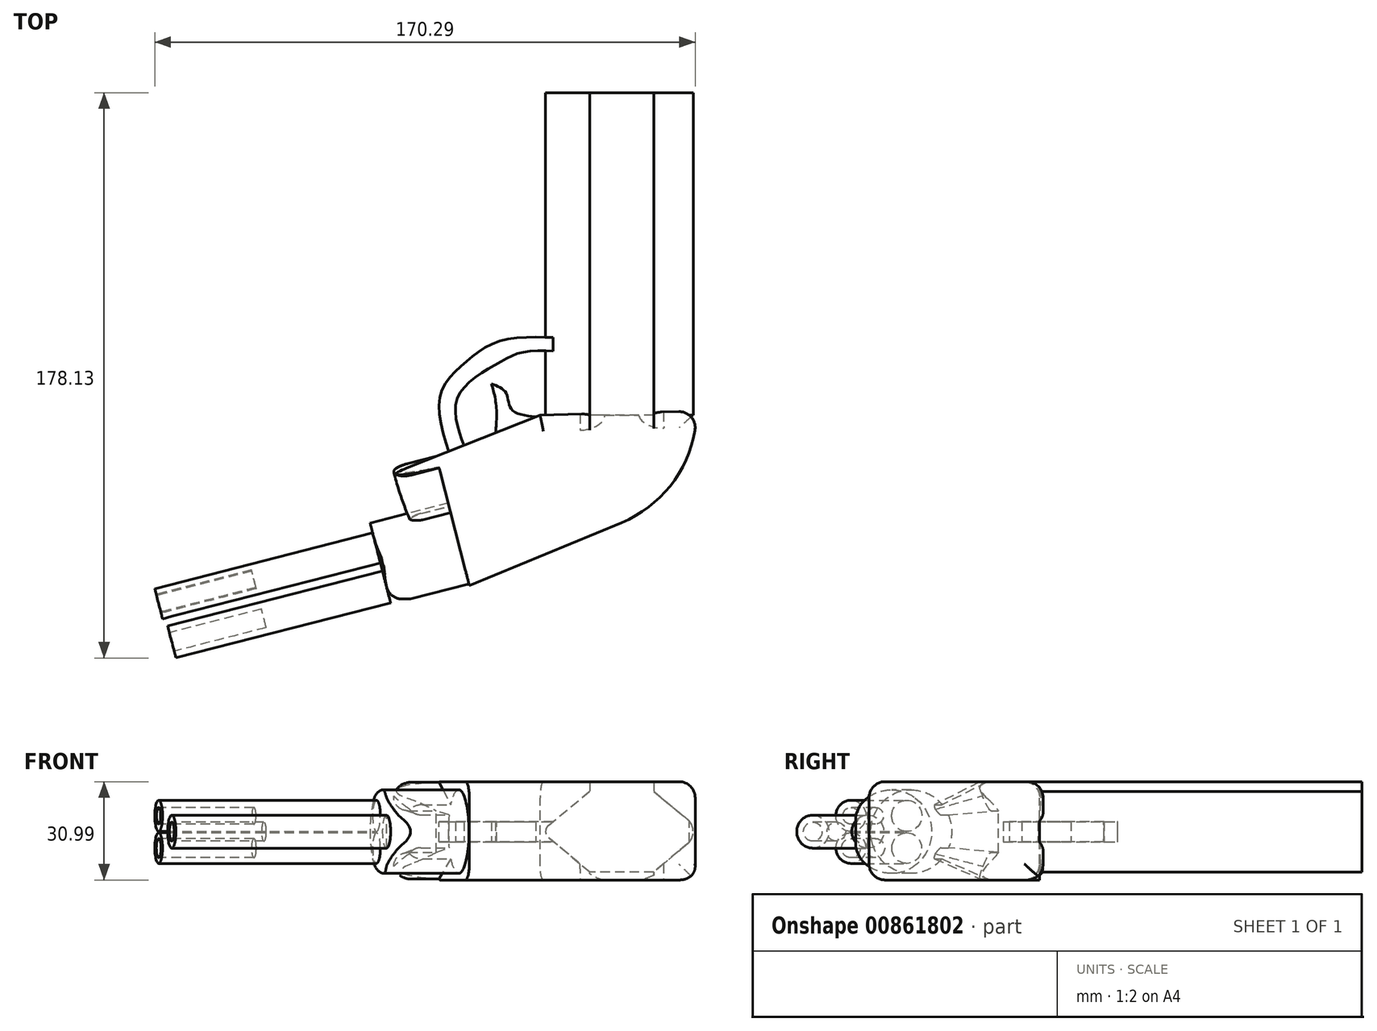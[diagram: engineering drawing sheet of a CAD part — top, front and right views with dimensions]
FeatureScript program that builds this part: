
annotation { "Feature Type Name" : "Feature", "Feature Type Description" : "" }
export const myFeature = defineFeature(function(context is Context, id is Id, definition is map)
    precondition{}
    {
        {
            var Q0;
            Q0=qCreatedBy(makeId("Front.planeOp"),FACE);
            var sketch = newSketch(context, id + "F0", { "sketchPlane" : qUnion([Q0])});
            skLineSegment(sketch, "E0", {"start": v(-10.1, 12.7) * mm, "end": v(10.1, 12.7) * mm});
            skLineSegment(sketch, "E1", {"start": v(10.1, 12.7) * mm, "end": v(25.4, 0) * mm});
            skLineSegment(sketch, "E2", {"start": v(25.4, 0) * mm, "end": v(10.1, -12.7) * mm});
            skLineSegment(sketch, "E3", {"start": v(10.1, -12.7) * mm, "end": v(-10.1, -12.7) * mm});
            skLineSegment(sketch, "E4", {"start": v(-10.1, -12.7) * mm, "end": v(-25.4, 0) * mm});
            skLineSegment(sketch, "E5", {"start": v(-25.4, 0) * mm, "end": v(-10.1, 12.7) * mm});
            skLineSegment(sketch, "E6", {"start": v(0, 12.7) * mm, "end": v(0, -12.7) * mm, "construction": true});
            skLineSegment(sketch, "E7", {"start": v(-25.4, 0) * mm, "end": v(25.4, 0) * mm, "construction": true});
            skSolve(sketch);
        }
        {
            var Q0;
            Q0=makeQuery(id+"F0.imprint","IMPRINT",FACE,{"disambiguationData":[TD([[makeQuery(id+"F0.imprint","IMPRINT",EDGE,{"derivedFrom":sQuery(id+"F0.wireOp",EDGE,"E0")}),-1.0]])]});
            extrude(context, id + "F1", {"entities" : qUnion([Q0]), "depth" : 101.6 * mm, "offsetDistance" : 25.4 * mm});
        }
        {
            var Q0;
            Q0=makeQuery(id+"F1.opExtrude","SWEPT_FACE",FACE,{"disambiguationData":[OSD([sQuery(id+"F0.wireOp",EDGE,"E0")])]});
            var sketch = newSketch(context, id + "F2", { "sketchPlane" : qUnion([Q0])});
            skLineSegment(sketch, "E8", {"start": v(-25.7, -101.58) * mm, "end": v(-77.82, -122.29) * mm});
            skLineSegment(sketch, "E9", {"start": v(-77.82, -122.29) * mm, "end": v(-81.03, -128.71) * mm});
            skLineSegment(sketch, "E10", {"start": v(-81.03, -128.71) * mm, "end": v(-73.12, -159.56) * mm});
            skLineSegment(sketch, "E11", {"start": v(-73.12, -159.56) * mm, "end": v(-58.16, -159.56) * mm});
            skLineSegment(sketch, "E12", {"start": v(-58.16, -159.56) * mm, "end": v(0, -135.46) * mm});
            skArc(sketch, "E13", {"start": v(0, -135.46) * mm, "mid": v(17.1, -121.47) * mm, "end": v(23.63, -100.35) * mm});
            skLineSegment(sketch, "E14", {"start": v(-25.7, -101.58) * mm, "end": v(23.63, -100.35) * mm});
            skSolve(sketch);
        }
        {
            var Q0;
            Q0=makeQuery(id+"F2.imprint","IMPRINT",FACE,{"disambiguationData":[TD([[makeQuery(id+"F2.imprint","IMPRINT",EDGE,{"derivedFrom":sQuery(id+"F2.wireOp",EDGE,"E8")}),1.0]])]});
            extrude(context, id + "F3", {"entities" : qUnion([Q0]), "operationType" : NewBodyOperationType.ADD, "oppositeDirection" : true, "depth" : 27.94 * mm, "offsetDistance" : 25.4 * mm});
        }
        {
            var Q0;
            Q0=makeQuery(id+"F3.opExtrude","CAP_FACE",FACE,{"disambiguationData":[OSD([sQuery(id+"F2.wireOp",EDGE,"E8"),sQuery(id+"F2.wireOp",EDGE,"E9"),sQuery(id+"F2.wireOp",EDGE,"E10"),sQuery(id+"F2.wireOp",EDGE,"E11"),sQuery(id+"F2.wireOp",EDGE,"E12"),sQuery(id+"F2.wireOp",EDGE,"E13"),sQuery(id+"F2.wireOp",EDGE,"E14")])],"isStart":true});
            extrude(context, id + "F4", {"entities" : qUnion([Q0]), "operationType" : NewBodyOperationType.ADD, "depth" : 3.05 * mm, "offsetDistance" : 25.4 * mm});
        }
        {
            var Q0;
            Q0=makeQuery(id+"F4.opExtrude","CAP_EDGE",EDGE,{"disambiguationData":[OSD([sQuery(id+"F2.wireOp",EDGE,"E14")])],"isStart":false});
            var Q1;
            Q1=makeQuery(id+"F4.opExtrude","CAP_EDGE",EDGE,{"disambiguationData":[OSD([sQuery(id+"F2.wireOp",EDGE,"E13")])],"isStart":false});
            var Q2;
            Q2=makeQuery(id+"F4.opExtrude","CAP_EDGE",EDGE,{"disambiguationData":[OSD([sQuery(id+"F2.wireOp",EDGE,"E8")])],"isStart":false});
            var Q3;
            Q3=makeQuery(id+"F4.opExtrude","CAP_EDGE",EDGE,{"disambiguationData":[OSD([sQuery(id+"F2.wireOp",EDGE,"E10")])],"isStart":false});
            var Q4;
            {var subQ0=sQuery(id+"F2.wireOp",EDGE,"E14");var subQ1=sQuery(id+"F2.wireOp",EDGE,"E13");Q4=makeQuery(id+"F4.boolean.opBoolean","MERGE",EDGE,{"derivedFrom":[makeQuery(id+"F3.opExtrude","SWEPT_EDGE",EDGE,{"disambiguationData":[OSD([subQ1,subQ0])]}),makeQuery(id+"F4.opExtrude","SWEPT_EDGE",EDGE,{"disambiguationData":[OSD([subQ1,subQ0])]})]});}
            var Q5;
            Q5=makeQuery(id+"F3.opExtrude","CAP_EDGE",EDGE,{"disambiguationData":[OSD([sQuery(id+"F2.wireOp",EDGE,"E14")])],"isStart":false});
            var Q6;
            Q6=makeQuery(id+"F3.opExtrude","CAP_EDGE",EDGE,{"disambiguationData":[OSD([sQuery(id+"F2.wireOp",EDGE,"E13")])],"isStart":false});
            var Q7;
            Q7=makeQuery(id+"F3.opExtrude","CAP_EDGE",EDGE,{"disambiguationData":[OSD([sQuery(id+"F2.wireOp",EDGE,"E10")])],"isStart":false});
            var Q8;
            Q8=makeQuery(id+"F3.opExtrude","CAP_EDGE",EDGE,{"disambiguationData":[OSD([sQuery(id+"F2.wireOp",EDGE,"E8")])],"isStart":false});
            var Q9;
            {var subQ0=sQuery(id+"F2.wireOp",EDGE,"E11");Q9=makeQuery(id+"F4.boolean.opBoolean","MERGE",FACE,{"derivedFrom":[makeQuery(id+"F3.opExtrude","SWEPT_FACE",FACE,{"disambiguationData":[OSD([subQ0])]}),makeQuery(id+"F4.opExtrude","SWEPT_FACE",FACE,{"disambiguationData":[OSD([subQ0])]})]});}
            var Q10;
            {var subQ0=sQuery(id+"F2.wireOp",EDGE,"E12");Q10=makeQuery(id+"F4.boolean.opBoolean","MERGE",FACE,{"derivedFrom":[makeQuery(id+"F3.opExtrude","SWEPT_FACE",FACE,{"disambiguationData":[OSD([subQ0])]}),makeQuery(id+"F4.opExtrude","SWEPT_FACE",FACE,{"disambiguationData":[OSD([subQ0])]})]});}
            var Q11;
            {var subQ0=sQuery(id+"F2.wireOp",EDGE,"E10");Q11=makeQuery(id+"F4.boolean.opBoolean","MERGE",FACE,{"derivedFrom":[makeQuery(id+"F3.opExtrude","SWEPT_FACE",FACE,{"disambiguationData":[OSD([subQ0])]}),makeQuery(id+"F4.opExtrude","SWEPT_FACE",FACE,{"disambiguationData":[OSD([subQ0])]})]});}
            fillet(context, id + "F5", {"entities" : qUnion([Q0, Q1, Q2, Q3, Q4, Q5, Q6, Q7, Q8, Q9, Q10, Q11]), "radius" : 5.08 * mm, "tangentPropagation" : true, "allowEdgeOverflow" : false});
        }
        {
            var Q0;
            {var subQ0=sQuery(id+"F2.wireOp",EDGE,"E10");Q0=makeQuery(id+"F4.boolean.opBoolean","MERGE",FACE,{"derivedFrom":[makeQuery(id+"F3.opExtrude","SWEPT_FACE",FACE,{"disambiguationData":[OSD([subQ0])]}),makeQuery(id+"F4.opExtrude","SWEPT_FACE",FACE,{"disambiguationData":[OSD([subQ0])]})]});}
            var sketch = newSketch(context, id + "F6", { "sketchPlane" : qUnion([Q0])});
            skCircle(sketch, "E15", {"center": v(132.45, 0) * mm, "radius": 5.2 * mm});
            skSolve(sketch);
        }
        {
            var Q0;
            {var subQ0=sQuery(id+"F6.wireOp",EDGE,"E15");var subQ1=sQuery(id+"F2.wireOp",EDGE,"E11");var subQ2=sQuery(id+"F2.wireOp",EDGE,"E10");var subQ3=makeQuery(id+"F4.boolean.opBoolean","MERGE",EDGE,{"derivedFrom":[makeQuery(id+"F3.opExtrude","SWEPT_EDGE",EDGE,{"disambiguationData":[OSD([subQ2,subQ1])]}),makeQuery(id+"F4.opExtrude","SWEPT_EDGE",EDGE,{"disambiguationData":[OSD([subQ2,subQ1])]})]});var subQ4=makeQuery(id+"F6.imprint","INTERSECT",VERTEX,{"disambiguationData":[OD(0.0)],"derivedFrom":[subQ3,subQ0]});Q0=makeQuery(id+"F6.imprint","IMPRINT",FACE,{"disambiguationData":[TD([[makeQuery(id+"F6.imprint","IMPRINT",EDGE,{"disambiguationData":[TD([[subQ4,1.0]])],"derivedFrom":subQ0}),1.0]])]});}
            var Q1;
            {var subQ0=sQuery(id+"F6.wireOp",EDGE,"E15");var subQ1=sQuery(id+"F2.wireOp",EDGE,"E10");var subQ2=sQuery(id+"F2.wireOp",EDGE,"E11");var subQ3=makeQuery(id+"F5.opFillet","BLEND_EDGE",EDGE,{"blendedFrom":[makeQuery(id+"F4.boolean.opBoolean","MERGE",EDGE,{"derivedFrom":[makeQuery(id+"F3.opExtrude","SWEPT_EDGE",EDGE,{"disambiguationData":[OSD([subQ1,subQ2])]}),makeQuery(id+"F4.opExtrude","SWEPT_EDGE",EDGE,{"disambiguationData":[OSD([subQ1,subQ2])]})]}),makeQuery(id+"F4.boolean.opBoolean","MERGE",FACE,{"derivedFrom":[makeQuery(id+"F3.opExtrude","SWEPT_FACE",FACE,{"disambiguationData":[OSD([subQ1])]}),makeQuery(id+"F4.opExtrude","SWEPT_FACE",FACE,{"disambiguationData":[OSD([subQ1])]})]})],"blendedInto":[makeQuery(id+"F4.boolean.opBoolean","MERGE",FACE,{"derivedFrom":[makeQuery(id+"F3.opExtrude","SWEPT_FACE",FACE,{"disambiguationData":[OSD([subQ1])]}),makeQuery(id+"F4.opExtrude","SWEPT_FACE",FACE,{"disambiguationData":[OSD([subQ1])]})]})]});var subQ4=makeQuery(id+"F6.imprint","INTERSECT",VERTEX,{"disambiguationData":[OD(0.0)],"derivedFrom":[subQ3,subQ0]});Q1=makeQuery(id+"F6.imprint","IMPRINT",FACE,{"disambiguationData":[TD([[makeQuery(id+"F6.imprint","IMPRINT",EDGE,{"disambiguationData":[TD([[subQ4,-1.0]])],"derivedFrom":subQ0}),1.0]])]});}
            extrude(context, id + "F7", {"entities" : qUnion([Q0, Q1]), "operationType" : NewBodyOperationType.ADD, "depth" : 69.85 * mm, "offsetDistance" : 25.4 * mm});
        }
        {
            var Q0;
            {var subQ0=sQuery(id+"F2.wireOp",EDGE,"E10");Q0=makeQuery(id+"F4.boolean.opBoolean","MERGE",FACE,{"derivedFrom":[makeQuery(id+"F3.opExtrude","SWEPT_FACE",FACE,{"disambiguationData":[OSD([subQ0])]}),makeQuery(id+"F4.opExtrude","SWEPT_FACE",FACE,{"disambiguationData":[OSD([subQ0])]})]});}
            var sketch = newSketch(context, id + "F8", { "sketchPlane" : qUnion([Q0])});
            skCircle(sketch, "E16", {"center": v(119.78, 4.99) * mm, "radius": 4.9 * mm});
            skCircle(sketch, "E17", {"center": v(119.78, -5.19) * mm, "radius": 4.84 * mm});
            skSolve(sketch);
        }
        {
            var Q0;
            Q0 = qSketchRegion(id + "F8", true);
            extrude(context, id + "F9", {"entities" : qUnion([Q0]), "operationType" : NewBodyOperationType.ADD, "depth" : 70.87 * mm, "offsetDistance" : 25.4 * mm});
        }
        {
            var Q0;
            {var subQ0=sQuery(id+"F2.wireOp",EDGE,"E10");Q0=makeQuery(id+"F4.boolean.opBoolean","MERGE",FACE,{"derivedFrom":[makeQuery(id+"F3.opExtrude","SWEPT_FACE",FACE,{"disambiguationData":[OSD([subQ0])]}),makeQuery(id+"F4.opExtrude","SWEPT_FACE",FACE,{"disambiguationData":[OSD([subQ0])]})]});}
            var sketch = newSketch(context, id + "F10", { "sketchPlane" : qUnion([Q0])});
            skCircle(sketch, "E18", {"center": v(124.86, 0) * mm, "radius": 13.17 * mm});
            skPoint(sketch, "E18.centerSnap0", {"position": v(115.56, 0) * mm});
            skCircle(sketch, "E19", {"center": v(124.86, 0) * mm, "radius": 29.12 * mm});
            skSolve(sketch);
        }
        {
            var Q0;
            Q0=makeQuery(id+"F10.imprint","IMPRINT",FACE,{"disambiguationData":[TD([[makeQuery(id+"F10.imprint","IMPRINT",EDGE,{"derivedFrom":sQuery(id+"F10.wireOp",EDGE,"E19")}),1.0]])]});
            var Q1;
            {var subQ1=sQuery(id+"F2.wireOp",EDGE,"E10");var subQ2=makeQuery(id+"F4.boolean.opBoolean","MERGE",FACE,{"derivedFrom":[makeQuery(id+"F3.opExtrude","SWEPT_FACE",FACE,{"disambiguationData":[OSD([subQ1])]}),makeQuery(id+"F4.opExtrude","SWEPT_FACE",FACE,{"disambiguationData":[OSD([subQ1])]})]});var subQ7=sQuery(id+"F2.wireOp",EDGE,"E9");var subQ8=makeQuery(id+"F5.opFillet","BLEND_EDGE",EDGE,{"blendedFrom":[makeQuery(id+"F4.boolean.opBoolean","MERGE",EDGE,{"derivedFrom":[makeQuery(id+"F3.opExtrude","SWEPT_EDGE",EDGE,{"disambiguationData":[OSD([subQ7,subQ1])]}),makeQuery(id+"F4.opExtrude","SWEPT_EDGE",EDGE,{"disambiguationData":[OSD([subQ7,subQ1])]})]}),subQ2],"blendedInto":[subQ2]});Q1=makeQuery(id+"F10.imprint","IMPRINT",FACE,{"disambiguationData":[TD([[makeQuery(id+"F10.imprint","IMPRINT",EDGE,{"derivedFrom":subQ8}),1.0]])]});}
            extrude(context, id + "F11", {"entities" : qUnion([Q0, Q1]), "operationType" : NewBodyOperationType.REMOVE, "oppositeDirection" : true, "depth" : 25.4 * mm, "offsetDistance" : 25.4 * mm});
        }
        {
            var Q0;
            Q0=makeQuery(id+"F11.boolean.opBoolean","COPY",FACE,{"derivedFrom":makeQuery(id+"F11.opExtrude","CAP_FACE",FACE,{"disambiguationData":[OSD([sQuery(id+"F10.wireOp",EDGE,"E18"),sQuery(id+"F10.wireOp",EDGE,"E19")])],"isStart":false})});
            var sketch = newSketch(context, id + "F12", { "sketchPlane" : qUnion([Q0])});
            skLineSegment(sketch, "E20", {"start": v(100.24, 15.56) * mm, "end": v(114.79, 8.5) * mm});
            skLineSegment(sketch, "E21", {"start": v(114.79, 8.5) * mm, "end": v(112.8, 5.3) * mm});
            skLineSegment(sketch, "E22", {"start": v(112.8, 5.3) * mm, "end": v(96.48, 6.57) * mm});
            skArc(sketch, "E23.0", {"start": v(100.24, 15.56) * mm, "mid": v(98.88, 13.17) * mm, "end": v(97.76, 10.67) * mm});
            skPoint(sketch, "E24.0", {"position": v(97.1, 8.84) * mm});
            skArc(sketch, "E25.0", {"start": v(97.76, 10.67) * mm, "mid": v(97.04, 8.64) * mm, "end": v(96.48, 6.57) * mm});
            skLineSegment(sketch, "E26", {"start": v(96.48, -6.57) * mm, "end": v(112.7, -5.08) * mm});
            skPoint(sketch, "E26.endSnap0", {"position": v(101.6, -5.08) * mm});
            skLineSegment(sketch, "E27", {"start": v(112.7, -5.08) * mm, "end": v(114.85, -8.57) * mm});
            skLineSegment(sketch, "E28", {"start": v(114.85, -8.57) * mm, "end": v(99.85, -14.93) * mm});
            skArc(sketch, "E29.0", {"start": v(97.56, -10.16) * mm, "mid": v(98.6, -12.6) * mm, "end": v(99.85, -14.93) * mm});
            skArc(sketch, "E30.0", {"start": v(96.48, -6.57) * mm, "mid": v(96.96, -8.38) * mm, "end": v(97.56, -10.16) * mm});
            skSolve(sketch);
        }
        {
            var Q0;
            {var subQ1=sQuery(id+"F12.wireOp",EDGE,"E20");Q0=makeQuery(id+"F12.imprint","IMPRINT",FACE,{"disambiguationData":[TD([[makeQuery(id+"F12.imprint","IMPRINT",EDGE,{"derivedFrom":subQ1}),-1.0]])]});}
            var Q1;
            {var subQ1=sQuery(id+"F12.wireOp",EDGE,"E26");Q1=makeQuery(id+"F12.imprint","IMPRINT",FACE,{"disambiguationData":[TD([[makeQuery(id+"F12.imprint","IMPRINT",EDGE,{"derivedFrom":subQ1}),-1.0]])]});}
            extrude(context, id + "F13", {"entities" : qUnion([Q0, Q1]), "operationType" : NewBodyOperationType.ADD, "depth" : 14.22 * mm, "offsetDistance" : 25.4 * mm});
        }
        {
            var Q0;
            Q0=makeQuery(id+"F13.opExtrude","CAP_EDGE",EDGE,{"disambiguationData":[OSD([sQuery(id+"F12.wireOp",EDGE,"E28")])],"isStart":false});
            var Q1;
            Q1=makeQuery(id+"F13.opExtrude","CAP_EDGE",EDGE,{"disambiguationData":[OSD([sQuery(id+"F12.wireOp",EDGE,"E26")])],"isStart":false});
            var Q2;
            Q2=makeQuery(id+"F13.opExtrude","CAP_EDGE",EDGE,{"disambiguationData":[OSD([sQuery(id+"F12.wireOp",EDGE,"E22")])],"isStart":false});
            var Q3;
            Q3=makeQuery(id+"F13.opExtrude","CAP_EDGE",EDGE,{"disambiguationData":[OSD([sQuery(id+"F12.wireOp",EDGE,"E20")])],"isStart":false});
            fillet(context, id + "F14", {"entities" : qUnion([Q0, Q1, Q2, Q3]), "radius" : 5.08 * mm, "tangentPropagation" : true, "allowEdgeOverflow" : false});
        }
        {
            var Q0;
            Q0=qCreatedBy(makeId("Top.planeOp"),FACE);
            var sketch = newSketch(context, id + "F15", { "sketchPlane" : qUnion([Q0])});
            skFitSpline(sketch, "E31", {"points": [v(-54.02, -114.78) * mm, v(-57.27, -95.86) * mm, v(-49.54, -85.26) * mm, v(-37.79, -78.1) * mm, v(-19.74, -77.24) * mm], "startDerivative": vector(-20.02, 65.56) * mm, "endDerivative": vector(53.45, -2.18) * mm});
            skLineSegment(sketch, "E32", {"start": v(-19.74, -77.24) * mm, "end": v(-19.74, -81.53) * mm});
            skFitSpline(sketch, "E33", {"points": [v(-19.74, -81.53) * mm, v(-29.76, -81.53) * mm, v(-36.35, -83.83) * mm, v(-45.52, -89.27) * mm, v(-51.83, -96.44) * mm, v(-51.54, -105.6) * mm, v(-48.87, -113.06) * mm], "startDerivative": vector(-32.94, 2.73) * mm, "endDerivative": vector(14.65, -33.68) * mm});
            skLineSegment(sketch, "E34", {"start": v(-48.87, -113.06) * mm, "end": v(-54.02, -114.78) * mm});
            skLineSegment(sketch, "E35", {"start": v(-19.74, -81.53) * mm, "end": v(-19.74, -77.24) * mm});
            skFitSpline(sketch, "E36", {"points": [v(-39.8, -107.9) * mm, v(-39.5, -99.01) * mm, v(-41.02, -91.74) * mm], "startDerivative": vector(1.53, 17.13) * mm, "endDerivative": vector(-3.99, 12.53) * mm});
            skFitSpline(sketch, "E37", {"points": [v(-41.02, -91.74) * mm, v(-36.43, -94.61) * mm, v(-34.33, -100.16) * mm, v(-21.67, -102.57) * mm], "startDerivative": vector(17.93, -6.63) * mm, "endDerivative": vector(24.68, -2.87) * mm});
            skLineSegment(sketch, "E38", {"start": v(-39.8, -107.9) * mm, "end": v(-21.67, -102.57) * mm});
            skSolve(sketch);
        }
        {
            var Q0;
            Q0=makeQuery(id+"F15.imprint","IMPRINT",FACE,{"disambiguationData":[TD([[makeQuery(id+"F15.imprint","IMPRINT",EDGE,{"derivedFrom":sQuery(id+"F15.wireOp",EDGE,"E31")}),-1.0]])]});
            var Q1;
            Q1=makeQuery(id+"F15.imprint","IMPRINT",FACE,{"disambiguationData":[TD([[makeQuery(id+"F15.imprint","IMPRINT",EDGE,{"derivedFrom":sQuery(id+"F15.wireOp",EDGE,"E36")}),-1.0]])]});
            extrude(context, id + "F16", {"entities" : qUnion([Q0, Q1]), "operationType" : NewBodyOperationType.ADD, "endBound" : BoundingType.SYMMETRIC, "depth" : 6.35 * mm, "offsetDistance" : 25.4 * mm});
        }
        {
            var Q0;
            Q0=makeQuery(id+"F7.opExtrude","CAP_FACE",FACE,{"disambiguationData":[OSD([sQuery(id+"F6.wireOp",EDGE,"E15")])],"isStart":false});
            var sketch = newSketch(context, id + "F17", { "sketchPlane" : qUnion([Q0])});
            skCircle(sketch, "E39", {"center": v(132.45, 0) * mm, "radius": 3 * mm});
            skCircle(sketch, "E40", {"center": v(119.78, -5.19) * mm, "radius": 3.03 * mm});
            skCircle(sketch, "E41", {"center": v(119.78, 4.99) * mm, "radius": 2.64 * mm});
            skSolve(sketch);
        }
        {
            var Q0;
            Q0 = qSketchRegion(id + "F17", true);
            extrude(context, id + "F18", {"entities" : qUnion([Q0]), "operationType" : NewBodyOperationType.REMOVE, "endBound" : BoundingType.SYMMETRIC, "oppositeDirection" : true, "depth" : 59.94 * mm, "offsetDistance" : 25.4 * mm});
        }
        {
            var Q0;
            Q0=makeQuery(id+"F1.opExtrude","SWEPT_EDGE",EDGE,{"disambiguationData":[OSD([sQuery(id+"F0.wireOp",EDGE,"E1"),sQuery(id+"F0.wireOp",EDGE,"E2")])]});
            fillet(context, id + "F19", {"entities" : qUnion([Q0]), "radius" : 5.08 * mm, "tangentPropagation" : true, "allowEdgeOverflow" : false});
        }
        {
            var Q0;
            {var subQ0=sQuery(id+"F0.wireOp",EDGE,"E0");var subQ1=sQuery(id+"F0.wireOp",EDGE,"E5");var subQ2=sQuery(id+"F0.wireOp",EDGE,"E4");Q0=makeQuery(id+"F16.boolean.opBoolean","SPLIT",EDGE,{"disambiguationData":[TD([makeQuery(id+"F4.opExtrude","SWEPT_FACE",FACE,{"disambiguationData":[OSD([subQ0])]})])],"derivedFrom":makeQuery(id+"F1.opExtrude","SWEPT_EDGE",EDGE,{"disambiguationData":[OSD([subQ2,subQ1])]})});}
            var Q1;
            {var subQ1=sQuery(id+"F0.wireOp",EDGE,"E5");var subQ3=sQuery(id+"F0.wireOp",EDGE,"E4");Q1=makeQuery(id+"F16.boolean.opBoolean","SPLIT",EDGE,{"disambiguationData":[TD([makeQuery(id+"F16.opExtrude","SWEPT_FACE",FACE,{"disambiguationData":[OSD([sQuery(id+"F15.wireOp",EDGE,"E33")])]})])],"derivedFrom":makeQuery(id+"F1.opExtrude","SWEPT_EDGE",EDGE,{"disambiguationData":[OSD([subQ3,subQ1])]})});}
            fillet(context, id + "F20", {"entities" : qUnion([Q0, Q1]), "radius" : 2.54 * mm, "tangentPropagation" : true, "allowEdgeOverflow" : false});
        }
    });
